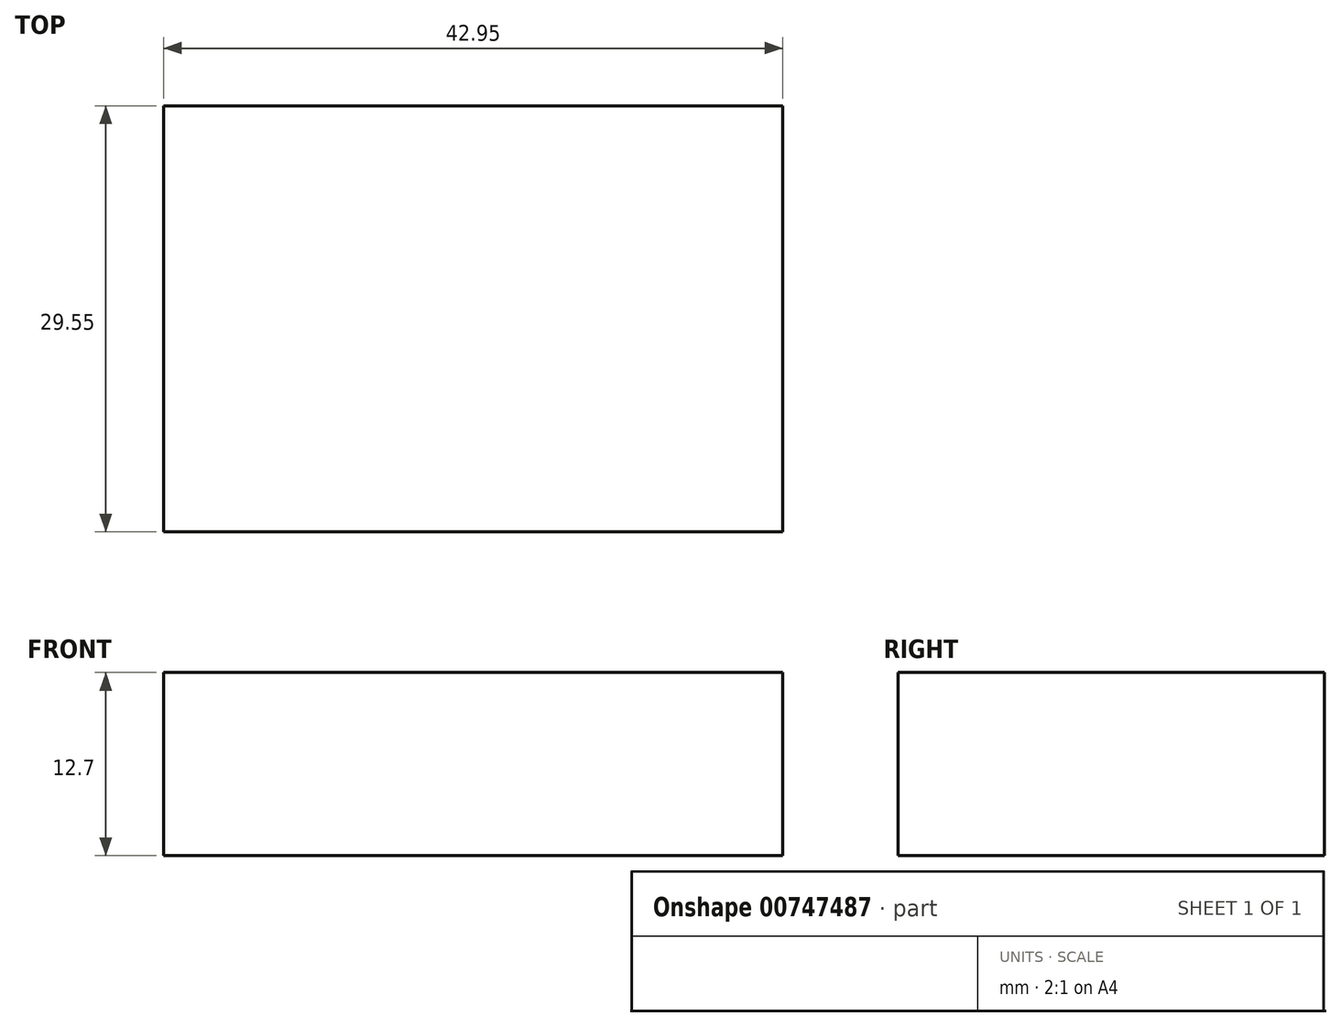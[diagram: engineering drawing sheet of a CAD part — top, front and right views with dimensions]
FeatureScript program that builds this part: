
annotation { "Feature Type Name" : "Feature", "Feature Type Description" : "" }
export const myFeature = defineFeature(function(context is Context, id is Id, definition is map)
    precondition{}
    {
        {
            var Q0;
            Q0=qCreatedBy(makeId("Top.planeOp"),FACE);
            var sketch = newSketch(context, id + "F0", { "sketchPlane" : qUnion([Q0])});
            skLineSegment(sketch, "E0.bottom", {"start": v(-42.95, 29.55) * mm, "end": v(0, 29.55) * mm});
            skLineSegment(sketch, "E0.top", {"start": v(-42.95, 0) * mm, "end": v(0, 0) * mm});
            skLineSegment(sketch, "E0.left", {"start": v(-42.95, 29.55) * mm, "end": v(-42.95, 0) * mm});
            skLineSegment(sketch, "E0.right", {"start": v(0, 29.55) * mm, "end": v(0, 0) * mm});
            skSolve(sketch);
        }
        {
            var Q0;
            Q0=makeQuery(id+"F0.imprint","IMPRINT",FACE,{"disambiguationData":[TD([[makeQuery(id+"F0.imprint","IMPRINT",EDGE,{"derivedFrom":sQuery(id+"F0.wireOp",EDGE,"E0.bottom")}),-1.0]])]});
            extrude(context, id + "F1", {"entities" : qUnion([Q0]), "depth" : 12.7 * mm, "offsetDistance" : 25.4 * mm});
        }
    });
